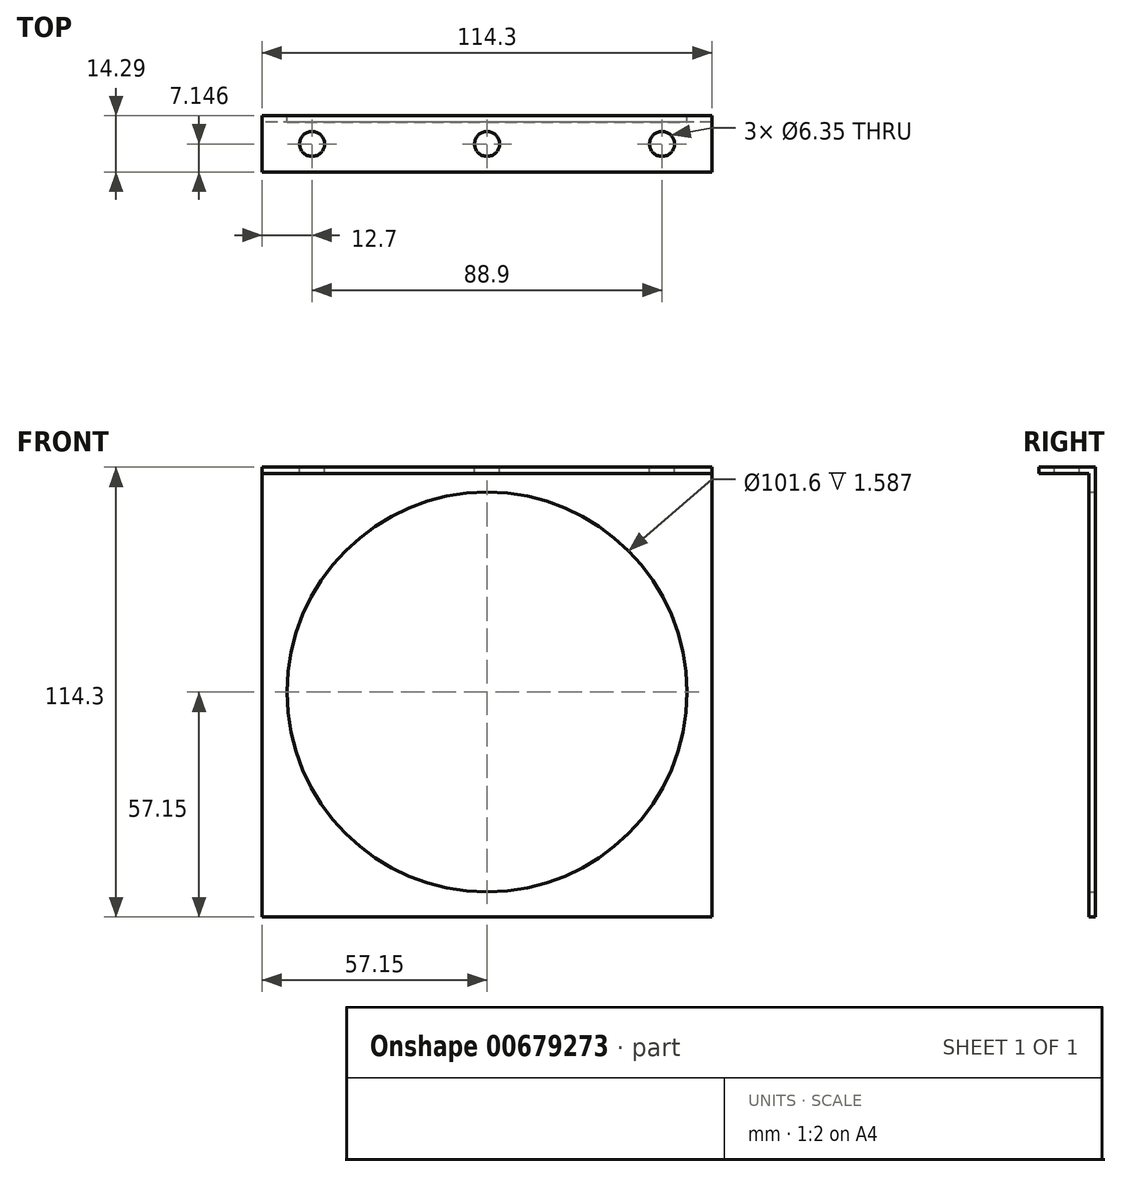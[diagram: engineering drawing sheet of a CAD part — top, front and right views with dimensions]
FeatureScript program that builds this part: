
annotation { "Feature Type Name" : "Feature", "Feature Type Description" : "" }
export const myFeature = defineFeature(function(context is Context, id is Id, definition is map)
    precondition{}
    {
        {
            var Q0;
            Q0=qCreatedBy(makeId("Front.planeOp"),FACE);
            var sketch = newSketch(context, id + "F0", { "sketchPlane" : qUnion([Q0])});
            skLineSegment(sketch, "E0.bottom", {"start": v(57.15, 57.15) * mm, "end": v(-57.15, 57.15) * mm});
            skLineSegment(sketch, "E0.top", {"start": v(57.15, -57.15) * mm, "end": v(-57.15, -57.15) * mm});
            skLineSegment(sketch, "E0.left", {"start": v(57.15, 57.15) * mm, "end": v(57.15, -57.15) * mm});
            skLineSegment(sketch, "E0.right", {"start": v(-57.15, 57.15) * mm, "end": v(-57.15, -57.15) * mm});
            skPoint(sketch, "E0.middle", {"position": v(0, 0) * mm});
            skCircle(sketch, "E1", {"center": v(0, 0) * mm, "radius": 50.8 * mm});
            skSolve(sketch);
        }
        {
            var Q0;
            Q0=qSketchRegion(id+"F0",true);
            extrude(context, id + "F1", {"entities" : qUnion([Q0]), "depth" : 1.59 * mm, "offsetDistance" : 25.4 * mm});
        }
        {
            var Q0;
            Q0=makeQuery(id+"F1.opExtrude","CAP_FACE",FACE,{"disambiguationData":[OSD([sQuery(id+"F0.wireOp",EDGE,"E0.bottom"),sQuery(id+"F0.wireOp",EDGE,"E0.top"),sQuery(id+"F0.wireOp",EDGE,"E0.left"),sQuery(id+"F0.wireOp",EDGE,"E0.right"),sQuery(id+"F0.wireOp",EDGE,"E1")])],"isStart":false});
            var sketch = newSketch(context, id + "F2", { "sketchPlane" : qUnion([Q0])});
            skLineSegment(sketch, "E2.bottom", {"start": v(-57.15, 57.15) * mm, "end": v(57.15, 57.15) * mm});
            skLineSegment(sketch, "E2.top", {"start": v(-57.15, 55.56) * mm, "end": v(57.15, 55.56) * mm});
            skLineSegment(sketch, "E2.left", {"start": v(-57.15, 57.15) * mm, "end": v(-57.15, 55.56) * mm});
            skLineSegment(sketch, "E2.right", {"start": v(57.15, 57.15) * mm, "end": v(57.15, 55.56) * mm});
            skSolve(sketch);
        }
        {
            var Q0;
            Q0=qSketchRegion(id+"F2",true);
            extrude(context, id + "F3", {"entities" : qUnion([Q0]), "operationType" : NewBodyOperationType.ADD, "depth" : 12.7 * mm, "offsetDistance" : 25.4 * mm});
        }
        {
            var Q0;
            Q0=makeQuery(id+"F3.boolean.opBoolean","MERGE",FACE,{"derivedFrom":[makeQuery(id+"F1.opExtrude","SWEPT_FACE",FACE,{"disambiguationData":[OSD([sQuery(id+"F0.wireOp",EDGE,"E0.bottom")])]}),makeQuery(id+"F3.opExtrude","SWEPT_FACE",FACE,{"disambiguationData":[OSD([sQuery(id+"F2.wireOp",EDGE,"E2.bottom")])]})]});
            var sketch = newSketch(context, id + "F4", { "sketchPlane" : qUnion([Q0])});
            skLineSegment(sketch, "E3", {"start": v(-57.15, -7.14) * mm, "end": v(57.15, -7.14) * mm});
            skCircle(sketch, "E4", {"center": v(0, -7.14) * mm, "radius": 3.18 * mm});
            skCircle(sketch, "E5", {"center": v(44.45, -7.14) * mm, "radius": 3.18 * mm});
            skCircle(sketch, "E6", {"center": v(-44.45, -7.14) * mm, "radius": 3.18 * mm});
            skSolve(sketch);
        }
        {
            var Q0;
            Q0=qSketchRegion(id+"F4",true);
            extrude(context, id + "F5", {"entities" : qUnion([Q0]), "operationType" : NewBodyOperationType.REMOVE, "oppositeDirection" : true, "depth" : 25.4 * mm, "offsetDistance" : 25.4 * mm});
        }
    });
